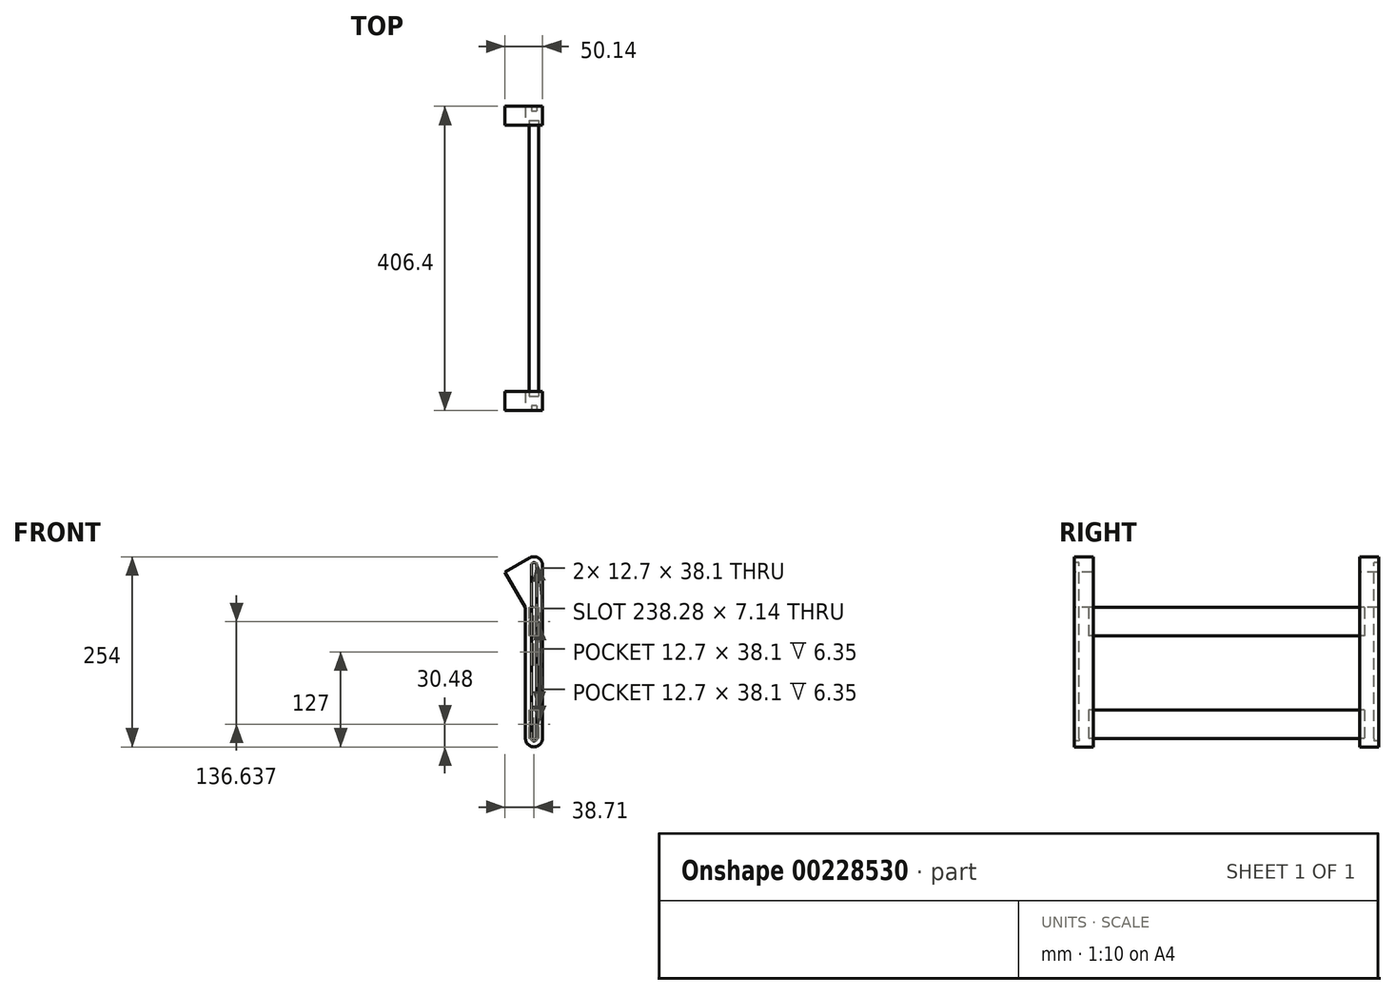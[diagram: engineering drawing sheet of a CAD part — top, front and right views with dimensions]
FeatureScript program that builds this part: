
annotation { "Feature Type Name" : "Feature", "Feature Type Description" : "" }
export const myFeature = defineFeature(function(context is Context, id is Id, definition is map)
    precondition{}
    {
        {
            var Q0;
            Q0=qCreatedBy(makeId("Front.planeOp"),FACE);
            var sketch = newSketch(context, id + "F0", { "sketchPlane" : qUnion([Q0])});
            skLineSegment(sketch, "E0", {"start": v(-11.43, 0) * mm, "end": v(-11.43, 174.74) * mm});
            skLineSegment(sketch, "E1", {"start": v(11.43, 231.14) * mm, "end": v(11.43, 0) * mm});
            skArc(sketch, "E2", {"start": v(-11.43, 0) * mm, "mid": v(0, -11.43) * mm, "end": v(11.43, 0) * mm});
            skLineSegment(sketch, "E3", {"start": v(-11.43, 174.74) * mm, "end": v(-38.71, 221.99) * mm});
            skLineSegment(sketch, "E4", {"start": v(-38.71, 221.99) * mm, "end": v(-5.72, 241.04) * mm});
            skArc(sketch, "E5", {"start": v(-5.72, 241.04) * mm, "mid": v(5.71, 241.04) * mm, "end": v(11.43, 231.14) * mm});
            skLineSegment(sketch, "E6", {"start": v(-3.57, 231.14) * mm, "end": v(-3.57, 0) * mm});
            skLineSegment(sketch, "E7", {"start": v(3.57, 0) * mm, "end": v(3.57, 231.14) * mm});
            skArc(sketch, "E8", {"start": v(-3.57, 231.14) * mm, "mid": v(0, 234.71) * mm, "end": v(3.57, 231.14) * mm});
            skArc(sketch, "E9", {"start": v(-3.57, 0) * mm, "mid": v(0, -3.57) * mm, "end": v(3.57, 0) * mm});
            skSolve(sketch);
        }
        {
            var Q0;
            Q0=makeQuery(id+"F0.imprint","IMPRINT",FACE,{"disambiguationData":[TD([[makeQuery(id+"F0.imprint","IMPRINT",EDGE,{"derivedFrom":sQuery(id+"F0.wireOp",EDGE,"E6")}),1.0]])]});
            var Q1;
            Q1=makeQuery(id+"F0.imprint","IMPRINT",FACE,{"disambiguationData":[TD([[makeQuery(id+"F0.imprint","IMPRINT",EDGE,{"derivedFrom":sQuery(id+"F0.wireOp",EDGE,"E0")}),-1.0]])]});
            extrude(context, id + "F1", {"entities" : qUnion([Q0, Q1]), "oppositeDirection" : true, "depth" : 25.4 * mm});
        }
        {
            var Q0;
            Q0 = qSketchRegion(id + "F0", true);
            var Q1;
            Q1=makeQuery(id+"F0.imprint","IMPRINT",FACE,{"disambiguationData":[TD([[makeQuery(id+"F0.imprint","IMPRINT",EDGE,{"derivedFrom":sQuery(id+"F0.wireOp",EDGE,"E6")}),1.0]])]});
            extrude(context, id + "F2", {"entities" : qUnion([Q0, Q1]), "oppositeDirection" : true, "depth" : 406.4 * mm, "hasSecondDirection" : true, "secondDirectionOppositeDirection" : true, "secondDirectionDepth" : 381 * mm});
        }
        {
            var Q0;
            Q0=makeQuery(id+"F1.opExtrude","CAP_FACE",FACE,{"disambiguationData":[OSD([sQuery(id+"F0.wireOp",EDGE,"E0"),sQuery(id+"F0.wireOp",EDGE,"E1"),sQuery(id+"F0.wireOp",EDGE,"E2"),sQuery(id+"F0.wireOp",EDGE,"E3"),sQuery(id+"F0.wireOp",EDGE,"E4"),sQuery(id+"F0.wireOp",EDGE,"E5")])],"isStart":false});
            var sketch = newSketch(context, id + "F3", { "sketchPlane" : qUnion([Q0])});
            skLineSegment(sketch, "E10", {"start": v(-6.35, 174.74) * mm, "end": v(-6.35, 136.64) * mm});
            skLineSegment(sketch, "E11", {"start": v(-6.35, 136.64) * mm, "end": v(6.35, 136.64) * mm});
            skLineSegment(sketch, "E12", {"start": v(6.35, 136.64) * mm, "end": v(6.35, 174.74) * mm});
            skLineSegment(sketch, "E13", {"start": v(6.35, 174.74) * mm, "end": v(-6.35, 174.74) * mm});
            skLineSegment(sketch, "E14", {"start": v(-6.35, 38.1) * mm, "end": v(-6.35, 0) * mm});
            skLineSegment(sketch, "E15", {"start": v(-6.35, 0) * mm, "end": v(6.35, 0) * mm});
            skLineSegment(sketch, "E16", {"start": v(6.35, 0) * mm, "end": v(6.35, 38.1) * mm});
            skLineSegment(sketch, "E17", {"start": v(6.35, 38.1) * mm, "end": v(-6.35, 38.1) * mm});
            skPoint(sketch, "E18", {"position": v(0, 0) * mm});
            skSolve(sketch);
        }
        {
            var Q0;
            Q0=makeQuery(id+"F3.imprint","IMPRINT",FACE,{"disambiguationData":[TD([[makeQuery(id+"F3.imprint","IMPRINT",EDGE,{"derivedFrom":sQuery(id+"F3.wireOp",EDGE,"E10")}),1.0]])]});
            var Q1;
            Q1=makeQuery(id+"F3.imprint","IMPRINT",FACE,{"disambiguationData":[TD([[makeQuery(id+"F3.imprint","IMPRINT",EDGE,{"derivedFrom":sQuery(id+"F3.wireOp",EDGE,"E14")}),1.0]])]});
            extrude(context, id + "F4", {"entities" : qUnion([Q0, Q1]), "depth" : 361.95 * mm, "hasSecondDirection" : true, "secondDirectionOppositeDirection" : true, "secondDirectionDepth" : 6.35 * mm});
        }
        {
            var Q0;
            Q0=makeQuery(id+"F4.opExtrude","SWEPT_BODY",BODY,{"disambiguationData":[OSD([sQuery(id+"F3.wireOp",EDGE,"E10"),sQuery(id+"F3.wireOp",EDGE,"E11"),sQuery(id+"F3.wireOp",EDGE,"E12"),sQuery(id+"F3.wireOp",EDGE,"E13")])]});
            var Q1;
            Q1=makeQuery(id+"F4.opExtrude","SWEPT_BODY",BODY,{"disambiguationData":[OSD([sQuery(id+"F3.wireOp",EDGE,"E14"),sQuery(id+"F3.wireOp",EDGE,"E15"),sQuery(id+"F3.wireOp",EDGE,"E16"),sQuery(id+"F3.wireOp",EDGE,"E17")])]});
            var Q2;
            Q2=makeQuery(id+"F2.opExtrude","SWEPT_BODY",BODY,{"disambiguationData":[OSD([sQuery(id+"F0.wireOp",EDGE,"E0"),sQuery(id+"F0.wireOp",EDGE,"E1"),sQuery(id+"F0.wireOp",EDGE,"E2"),sQuery(id+"F0.wireOp",EDGE,"E3"),sQuery(id+"F0.wireOp",EDGE,"E4"),sQuery(id+"F0.wireOp",EDGE,"E5")])]});
            var Q3;
            Q3=makeQuery(id+"F1.opExtrude","SWEPT_BODY",BODY,{"disambiguationData":[OSD([sQuery(id+"F0.wireOp",EDGE,"E0"),sQuery(id+"F0.wireOp",EDGE,"E1"),sQuery(id+"F0.wireOp",EDGE,"E2"),sQuery(id+"F0.wireOp",EDGE,"E3"),sQuery(id+"F0.wireOp",EDGE,"E4"),sQuery(id+"F0.wireOp",EDGE,"E5")])]});
            var Q4;
            Q4=makeQuery(id+"F4.opExtrude","SWEPT_FACE",FACE,{"disambiguationData":[OSD([sQuery(id+"F3.wireOp",EDGE,"E12")])]});
            var Q5;
            Q5=makeQuery(id+"F4.opExtrude","SWEPT_FACE",FACE,{"disambiguationData":[OSD([sQuery(id+"F3.wireOp",EDGE,"E13")])]});
            booleanBodies(context, id + "F5", {"operationType" : BooleanOperationType.SUBTRACTION, "tools" : qUnion([Q0, Q1]), "targets" : qUnion([Q2, Q3]), "entitiesToOffset" : qUnion([Q4, Q5]), "keepTools" : true});
        }
        {
            var Q0;
            Q0=makeQuery(id+"F0.imprint","IMPRINT",FACE,{"disambiguationData":[TD([[makeQuery(id+"F0.imprint","IMPRINT",EDGE,{"derivedFrom":sQuery(id+"F0.wireOp",EDGE,"E6")}),1.0]])]});
            extrude(context, id + "F6", {"entities" : qUnion([Q0]), "operationType" : NewBodyOperationType.REMOVE, "oppositeDirection" : true, "depth" : 6.35 * mm});
        }
        {
            var Q0;
            Q0=makeQuery(id+"F0.imprint","IMPRINT",FACE,{"disambiguationData":[TD([[makeQuery(id+"F0.imprint","IMPRINT",EDGE,{"derivedFrom":sQuery(id+"F0.wireOp",EDGE,"E6")}),1.0]])]});
            var Q1;
            Q1=makeQuery(id+"F2.opExtrude","CAP_FACE",FACE,{"disambiguationData":[OSD([sQuery(id+"F0.wireOp",EDGE,"E0"),sQuery(id+"F0.wireOp",EDGE,"E1"),sQuery(id+"F0.wireOp",EDGE,"E2"),sQuery(id+"F0.wireOp",EDGE,"E3"),sQuery(id+"F0.wireOp",EDGE,"E4"),sQuery(id+"F0.wireOp",EDGE,"E5")])],"isStart":false});
            extrude(context, id + "F7", {"entities" : qUnion([Q0]), "operationType" : NewBodyOperationType.REMOVE, "endBound" : BoundingType.UP_TO_SURFACE, "oppositeDirection" : true, "endBoundEntityFace" : qUnion([Q1]), "depth" : 25.4 * mm, "hasSecondDirection" : true, "secondDirectionOppositeDirection" : true, "secondDirectionDepth" : 400.05 * mm});
        }
    });
